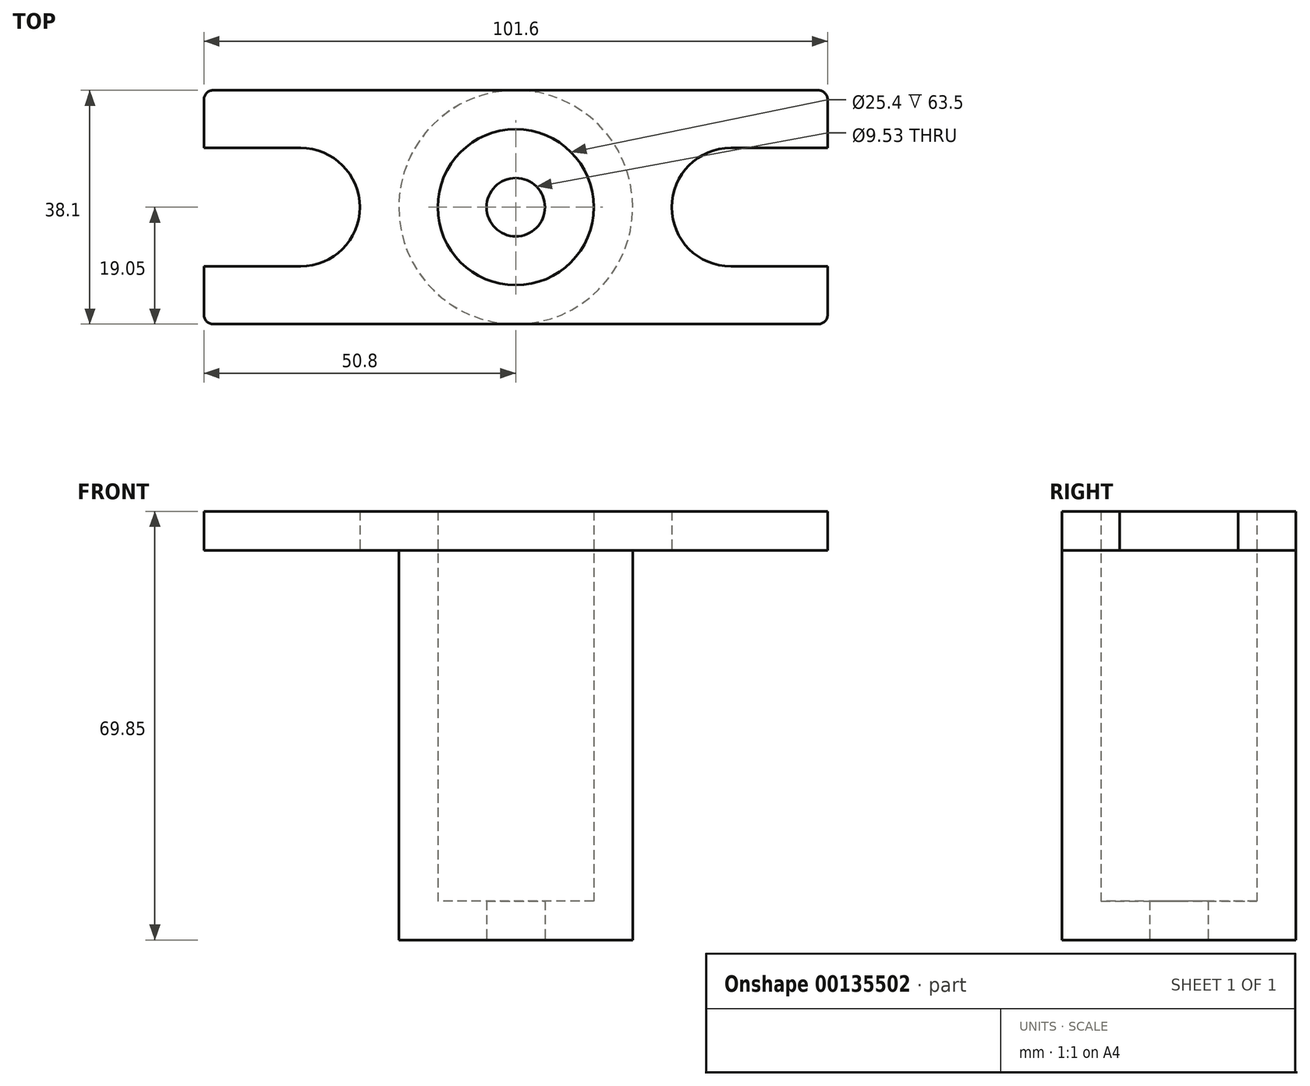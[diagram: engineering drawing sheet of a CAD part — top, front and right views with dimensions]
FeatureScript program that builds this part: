
annotation { "Feature Type Name" : "Feature", "Feature Type Description" : "" }
export const myFeature = defineFeature(function(context is Context, id is Id, definition is map)
    precondition{}
    {
        {
            var Q0;
            Q0=qCreatedBy(makeId("Top.planeOp"),FACE);
            var sketch = newSketch(context, id + "F0", { "sketchPlane" : qUnion([Q0])});
            skLineSegment(sketch, "E0.bottom", {"start": v(49.28, 19.05) * mm, "end": v(-49.28, 19.05) * mm});
            skLineSegment(sketch, "E0.top", {"start": v(49.28, -19.05) * mm, "end": v(-49.28, -19.05) * mm});
            skLineSegment(sketch, "E0.left", {"start": v(50.8, 17.53) * mm, "end": v(50.8, 9.65) * mm});
            skLineSegment(sketch, "E0.right", {"start": v(-50.8, 17.53) * mm, "end": v(-50.8, 9.65) * mm});
            skPoint(sketch, "E0.middle", {"position": v(0, 0) * mm});
            skCircle(sketch, "E1", {"center": v(0, 0) * mm, "radius": 12.7 * mm});
            skPoint(sketch, "E2.visualSharp", {"position": v(-50.8, 19.05) * mm});
            skArc(sketch, "E2.filletArc", {"start": v(-49.28, 19.05) * mm, "mid": v(-50.35, 18.6) * mm, "end": v(-50.8, 17.53) * mm});
            skPoint(sketch, "E3.visualSharp", {"position": v(50.8, 19.05) * mm});
            skArc(sketch, "E3.filletArc", {"start": v(50.8, 17.53) * mm, "mid": v(50.35, 18.6) * mm, "end": v(49.28, 19.05) * mm});
            skPoint(sketch, "E4.visualSharp", {"position": v(50.8, -19.05) * mm});
            skArc(sketch, "E4.filletArc", {"start": v(49.28, -19.05) * mm, "mid": v(50.35, -18.6) * mm, "end": v(50.8, -17.53) * mm});
            skPoint(sketch, "E5.visualSharp", {"position": v(-50.8, -19.05) * mm});
            skArc(sketch, "E5.filletArc", {"start": v(-50.8, -17.53) * mm, "mid": v(-50.35, -18.6) * mm, "end": v(-49.28, -19.05) * mm});
            skLineSegment(sketch, "E6", {"start": v(0, 0) * mm, "end": v(35.05, 0) * mm, "construction": true});
            skLineSegment(sketch, "E7", {"start": v(0, 0) * mm, "end": v(-35.05, 0) * mm, "construction": true});
            skArc(sketch, "E8", {"start": v(35.05, 9.65) * mm, "mid": v(25.4, 0) * mm, "end": v(35.05, -9.65) * mm});
            skArc(sketch, "E9", {"start": v(-35.05, -9.65) * mm, "mid": v(-25.4, 0) * mm, "end": v(-35.05, 9.65) * mm});
            skLineSegment(sketch, "E10", {"start": v(-35.05, 9.65) * mm, "end": v(-50.8, 9.65) * mm});
            skLineSegment(sketch, "E11", {"start": v(-35.05, -9.65) * mm, "end": v(-50.8, -9.65) * mm});
            skLineSegment(sketch, "E12", {"start": v(35.05, 9.65) * mm, "end": v(50.8, 9.65) * mm});
            skLineSegment(sketch, "E13", {"start": v(35.05, -9.65) * mm, "end": v(50.8, -9.65) * mm});
            skLineSegment(sketch, "E14.trimOffspring", {"start": v(50.8, -9.65) * mm, "end": v(50.8, -17.53) * mm});
            skLineSegment(sketch, "E15.trimOffspring", {"start": v(-50.8, -9.65) * mm, "end": v(-50.8, -17.53) * mm});
            skSolve(sketch);
        }
        {
            var Q0;
            Q0 = qSketchRegion(id + "F0", true);
            extrude(context, id + "F1", {"entities" : qUnion([Q0]), "depth" : 6.35 * mm});
        }
        {
            var Q0;
            Q0=makeQuery(id+"F1.opExtrude","CAP_FACE",FACE,{"disambiguationData":[OSD([sQuery(id+"F0.wireOp",EDGE,"E0.bottom"),sQuery(id+"F0.wireOp",EDGE,"E0.top"),sQuery(id+"F0.wireOp",EDGE,"E0.left"),sQuery(id+"F0.wireOp",EDGE,"E0.right"),sQuery(id+"F0.wireOp",EDGE,"E1"),sQuery(id+"F0.wireOp",EDGE,"E2.filletArc"),sQuery(id+"F0.wireOp",EDGE,"E3.filletArc"),sQuery(id+"F0.wireOp",EDGE,"E4.filletArc"),sQuery(id+"F0.wireOp",EDGE,"E5.filletArc"),sQuery(id+"F0.wireOp",EDGE,"E8"),sQuery(id+"F0.wireOp",EDGE,"E9"),sQuery(id+"F0.wireOp",EDGE,"E10"),sQuery(id+"F0.wireOp",EDGE,"E11"),sQuery(id+"F0.wireOp",EDGE,"E12"),sQuery(id+"F0.wireOp",EDGE,"E13"),sQuery(id+"F0.wireOp",EDGE,"E14.trimOffspring"),sQuery(id+"F0.wireOp",EDGE,"E15.trimOffspring")])],"isStart":true});
            var sketch = newSketch(context, id + "F2", { "sketchPlane" : qUnion([Q0])});
            skCircle(sketch, "E16", {"center": v(0, 0) * mm, "radius": 19.05 * mm});
            skSolve(sketch);
        }
        {
            var Q0;
            Q0 = qSketchRegion(id + "F2", true);
            extrude(context, id + "F3", {"entities" : qUnion([Q0]), "operationType" : NewBodyOperationType.ADD, "depth" : 63.5 * mm});
        }
        {
            var Q0;
            Q0=makeQuery(id+"F3.opExtrude","CAP_FACE",FACE,{"disambiguationData":[OSD([sQuery(id+"F2.wireOp",EDGE,"E16")])],"isStart":true});
            extrude(context, id + "F4", {"entities" : qUnion([Q0]), "operationType" : NewBodyOperationType.REMOVE, "oppositeDirection" : true, "depth" : 57.15 * mm});
        }
        {
            var Q0;
            Q0=makeQuery(id+"F3.opExtrude","CAP_FACE",FACE,{"disambiguationData":[OSD([sQuery(id+"F2.wireOp",EDGE,"E16")])],"isStart":false});
            var sketch = newSketch(context, id + "F5", { "sketchPlane" : qUnion([Q0])});
            skCircle(sketch, "E17", {"center": v(0, 0) * mm, "radius": 4.76 * mm});
            skSolve(sketch);
        }
        {
            var Q0;
            Q0 = qSketchRegion(id + "F5", true);
            extrude(context, id + "F6", {"entities" : qUnion([Q0]), "operationType" : NewBodyOperationType.REMOVE, "endBound" : BoundingType.THROUGH_ALL, "oppositeDirection" : true, "depth" : 25.4 * mm});
        }
    });
